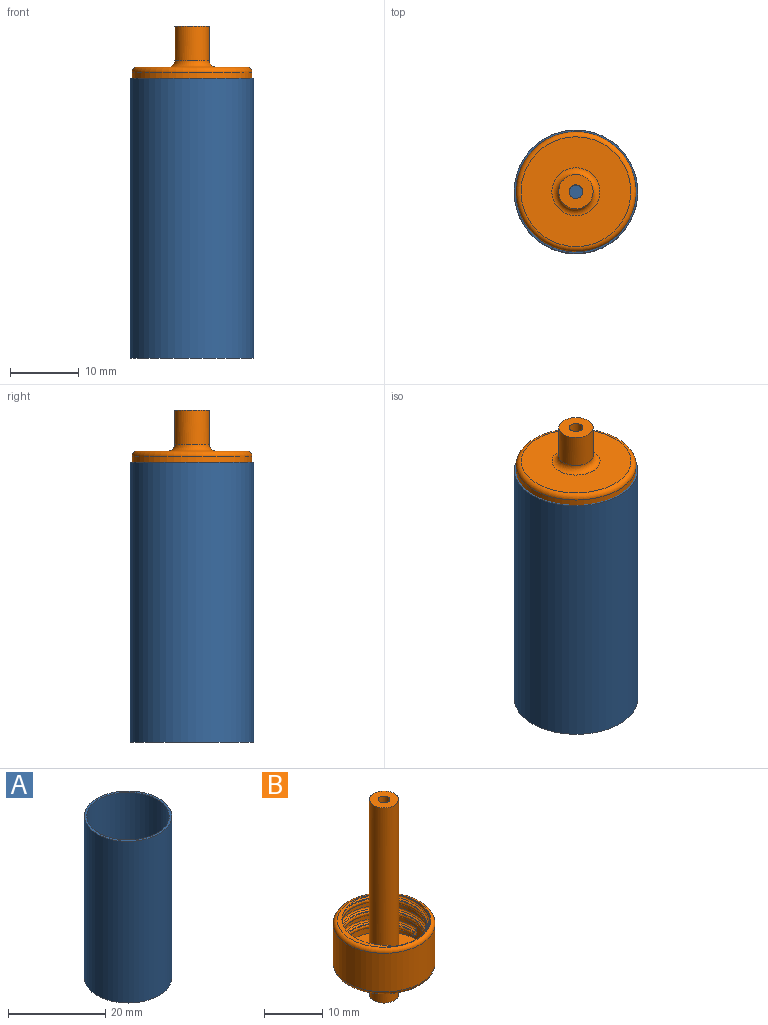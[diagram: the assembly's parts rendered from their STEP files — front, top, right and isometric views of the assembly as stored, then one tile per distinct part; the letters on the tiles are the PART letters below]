
ASSEMBLY  parts=2 mates=1
PART A: 5 faces, bbox 18x18x40.8 mm
  f0: cylinder r=9mm len=40.8mm, axis (0,0,-1), area 2307.2mm2, adj f1,f3
  f1: plane 18x18mm, normal (0,0,-1), area 254.5mm2, adj f0
  f2: cylinder r=8.5mm len=39.8mm, axis (0,0,-1), area 2125.6mm2, adj f3,f4
  f3: plane 18x18mm, normal (0,0,1), area 27.5mm2, adj f0,f2
  f4: plane 17x17mm, normal (0,0,1), area 227mm2, adj f2
PART B: 20 faces, bbox 19.4x19.4x41.5 mm
  f0: bspline ~18.24x15.8mm, area 36.6mm2, adj f2,f5,f9,f10
  f1: bspline ~18.24x15.8mm, area 31.7mm2, adj f3,f5,f7,f9
  f2: bspline ~14.85x14.84mm, area 14.4mm2, adj f0,f3,f5,f9
  f3: bspline ~15.34x15.32mm, area 136.3mm2, adj f1,f2,f5,f9
  f4: cylinder r=8.75mm len=17.5mm, axis (0,0,-1), area 445.3mm2, adj f11,f12
  f5: plane 16.46x16.46mm, normal (0,0,1), area 17.7mm2, adj f0,f1,f2,f3,f7,f10,f12
  f6: plane 16x16mm, normal (0,0,-1), area 162.6mm2, adj f11,f18
  f7: cylinder r=7.9mm len=15.8mm, axis (0,0,1), area 215mm2, adj f1,f5,f8,f9,f10
  f8: plane 15.8x15.8mm, normal (0,0,1), area 157.6mm2, adj f7,f19
  f9: plane 1.62x0.8mm, normal (0,-1,0), area 0.7mm2, adj f0,f1,f2,f3,f7,f10
  f10: bspline ~15.82x15.82mm, area 50mm2, adj f0,f5,f7,f9
  f11: torus R=8mm, axis (0,0,1), area 62.8mm2, adj f4,f6
  f12: torus R=8mm, axis (0,0,1), area 62.8mm2, adj f4,f5
  f13: plane 5x5mm, normal (0,0,1), area 16.5mm2, adj f14,f15
  f14: cylinder r=2.5mm len=32.4mm, axis (0,0,1), area 508.9mm2, adj f13,f19
  f15: cylinder r=1mm len=41mm, axis (0,0,-1), area 257.6mm2, adj f13,f17
  f16: cylinder r=2.5mm len=5mm, axis (0,0,1), area 78.5mm2, adj f17,f18
  f17: plane 5x5mm, normal (0,0,-1), area 16.5mm2, adj f15,f16
  f18: torus R=3.5mm, axis (0,0,1), area 28.3mm2, adj f6,f16
  f19: torus R=3.5mm, axis (0,0,1), area 28.3mm2, adj f8,f14
PLACE A t=(-22.98,-5.11,-8.16)mm
PLACE B rot(axis=(1,0,0),180deg) t=(-22.98,-5.11,34.24)mm
MATE fastened B.f4 <-> A.f0  axis (0,0,-1) through (-22.98,-5.11,32.64)mm
